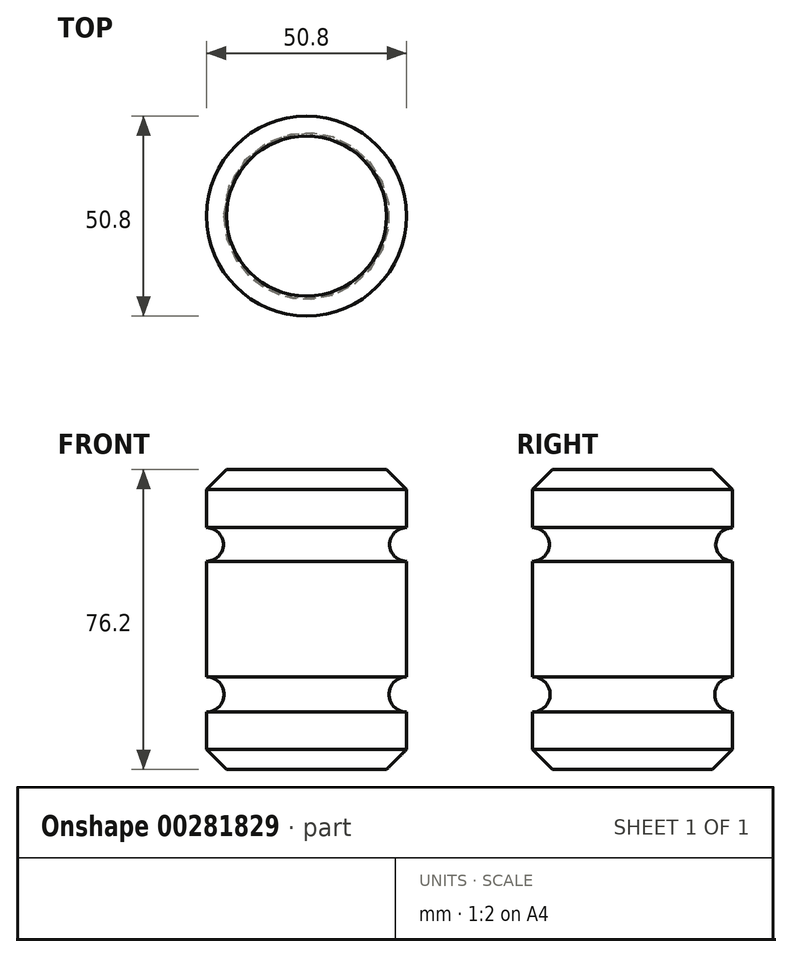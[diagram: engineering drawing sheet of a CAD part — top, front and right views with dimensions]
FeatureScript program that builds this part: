
annotation { "Feature Type Name" : "Feature", "Feature Type Description" : "" }
export const myFeature = defineFeature(function(context is Context, id is Id, definition is map)
    precondition{}
    {
        {
            var Q0;
            Q0=qCreatedBy(makeId("Front.planeOp"),FACE);
            var sketch = newSketch(context, id + "F0", { "sketchPlane" : qUnion([Q0])});
            skLineSegment(sketch, "E0.bottom", {"start": v(0, 0) * mm, "end": v(-25.4, 0) * mm});
            skLineSegment(sketch, "E0.top", {"start": v(0, 76.2) * mm, "end": v(-25.4, 76.2) * mm});
            skLineSegment(sketch, "E0.left", {"start": v(0, 0) * mm, "end": v(0, 14.58) * mm});
            skLineSegment(sketch, "E0.right", {"start": v(-25.4, 0) * mm, "end": v(-25.4, 76.2) * mm});
            skArc(sketch, "E1", {"start": v(0, 61.42) * mm, "mid": v(-4.27, 57.15) * mm, "end": v(0, 52.88) * mm});
            skArc(sketch, "E2", {"start": v(0, 23.52) * mm, "mid": v(-4.47, 19.05) * mm, "end": v(0, 14.58) * mm});
            skLineSegment(sketch, "E3.trimOffspring", {"start": v(0, 23.52) * mm, "end": v(0, 52.88) * mm});
            skLineSegment(sketch, "E4.trimOffspring", {"start": v(0, 61.42) * mm, "end": v(0, 76.2) * mm});
            skSolve(sketch);
        }
        {
            var Q0;
            Q0 = qSketchRegion(id + "F0", true);
            var Q1;
            Q1=sQuery(id+"F0.wireOp",EDGE,"E0.right");
            revolve(context, id + "F1", {"entities" : qUnion([Q0]), "axis" : qUnion([Q1]), "revolveType" : RevolveType.FULL});
        }
        {
            var Q0;
            Q0=makeQuery(id+"F1.opRevolve","SWEPT_EDGE",EDGE,{"disambiguationData":[OSD([sQuery(id+"F0.wireOp",EDGE,"E0.bottom"),sQuery(id+"F0.wireOp",EDGE,"E0.left")])]});
            var Q1;
            Q1=makeQuery(id+"F1.opRevolve","SWEPT_EDGE",EDGE,{"disambiguationData":[OSD([sQuery(id+"F0.wireOp",EDGE,"E0.top"),sQuery(id+"F0.wireOp",EDGE,"E4.trimOffspring")])]});
            chamfer(context, id + "F2", {"entities" : qUnion([Q0, Q1]), "width" : 5.08 * mm, "tangentPropagation" : true});
        }
    });
